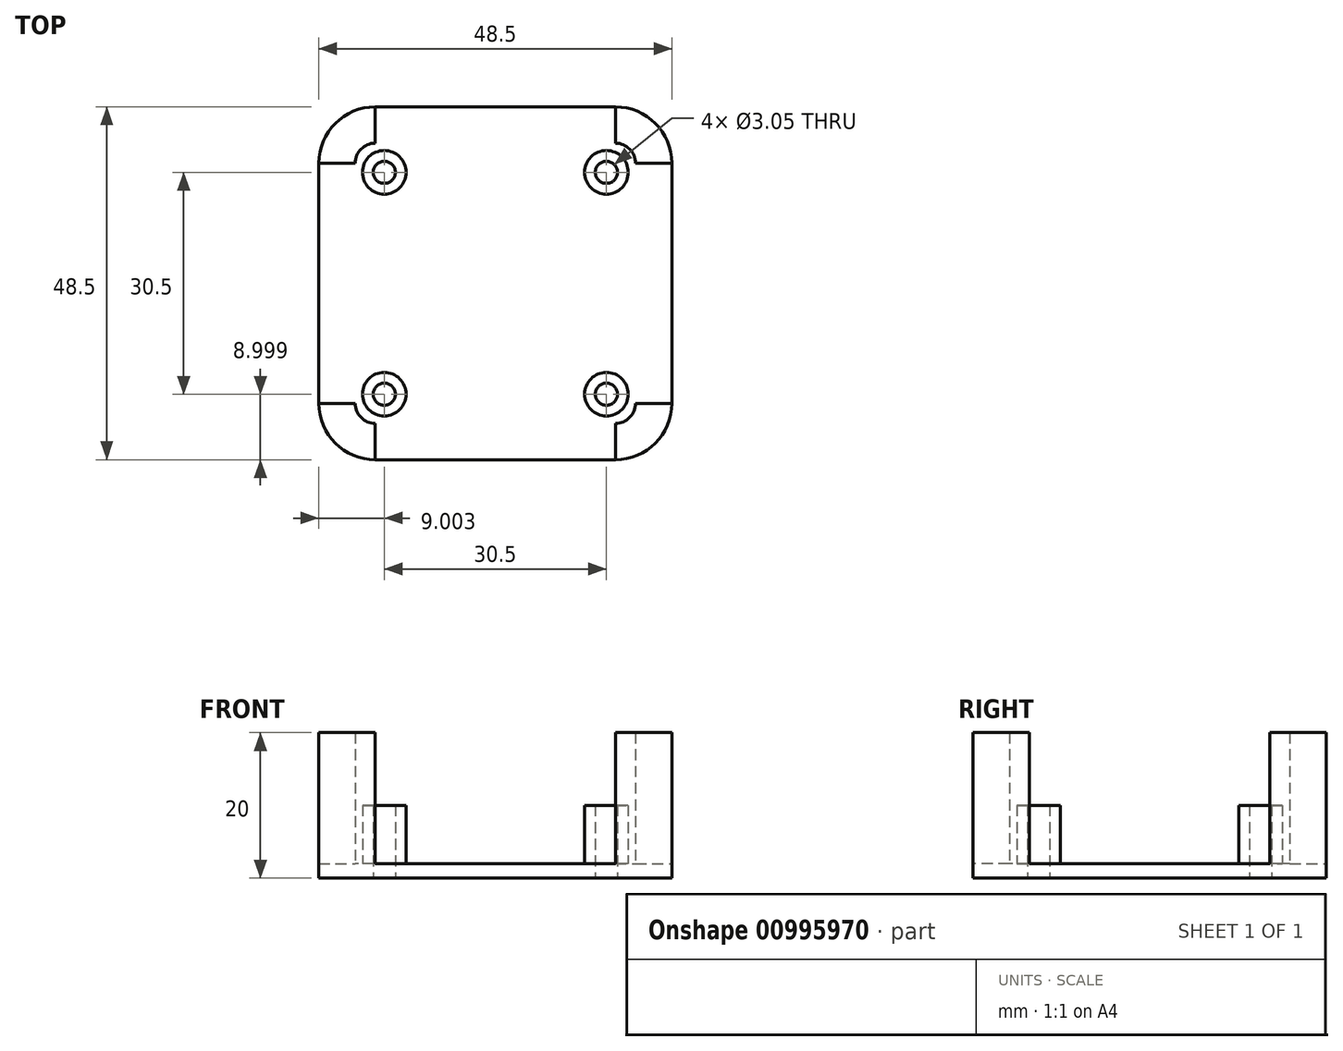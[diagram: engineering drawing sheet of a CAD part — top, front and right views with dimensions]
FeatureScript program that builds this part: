
annotation { "Feature Type Name" : "Feature", "Feature Type Description" : "" }
export const myFeature = defineFeature(function(context is Context, id is Id, definition is map)
    precondition{}
    {
        {
            var Q0;
            Q0=qCreatedBy(makeId("Top.planeOp"),FACE);
            var sketch = newSketch(context, id + "F0", { "sketchPlane" : qUnion([Q0])});
            skLineSegment(sketch, "E0.bottom", {"start": v(-15.03, 16.3) * mm, "end": v(17.97, 16.3) * mm});
            skLineSegment(sketch, "E0.top", {"start": v(-15.03, -22.2) * mm, "end": v(17.97, -22.2) * mm});
            skLineSegment(sketch, "E0.left", {"start": v(-17.78, 13.55) * mm, "end": v(-17.78, -19.45) * mm});
            skLineSegment(sketch, "E0.right", {"start": v(20.72, 13.55) * mm, "end": v(20.72, -19.45) * mm});
            skLineSegment(sketch, "E1.0", {"start": v(-13.78, 12.3) * mm, "end": v(-13.78, -18.2) * mm, "construction": true});
            skLineSegment(sketch, "E1.1", {"start": v(-13.78, 12.3) * mm, "end": v(16.72, 12.3) * mm, "construction": true});
            skLineSegment(sketch, "E1.2", {"start": v(16.72, 12.3) * mm, "end": v(16.72, -18.2) * mm, "construction": true});
            skLineSegment(sketch, "E1.3", {"start": v(-13.78, -18.2) * mm, "end": v(16.72, -18.2) * mm, "construction": true});
            skPoint(sketch, "E2.visualSharp", {"position": v(-17.78, 16.3) * mm});
            skArc(sketch, "E2.filletArc", {"start": v(-15.03, 16.3) * mm, "mid": v(-16.97, 15.5) * mm, "end": v(-17.78, 13.55) * mm});
            skPoint(sketch, "E3.visualSharp", {"position": v(20.72, 16.3) * mm});
            skArc(sketch, "E3.filletArc", {"start": v(20.72, 13.55) * mm, "mid": v(19.92, 15.5) * mm, "end": v(17.97, 16.3) * mm});
            skPoint(sketch, "E4.visualSharp", {"position": v(20.72, -22.2) * mm});
            skArc(sketch, "E4.filletArc", {"start": v(17.97, -22.2) * mm, "mid": v(19.92, -21.4) * mm, "end": v(20.72, -19.45) * mm});
            skPoint(sketch, "E5.visualSharp", {"position": v(-17.78, -22.2) * mm});
            skArc(sketch, "E5.filletArc", {"start": v(-17.78, -19.45) * mm, "mid": v(-16.97, -21.4) * mm, "end": v(-15.03, -22.2) * mm});
            skLineSegment(sketch, "E6.0", {"start": v(-22.78, 13.55) * mm, "end": v(-22.78, -19.45) * mm});
            skArc(sketch, "E6.1", {"start": v(-15.03, 21.3) * mm, "mid": v(-20.5, 19.03) * mm, "end": v(-22.78, 13.55) * mm});
            skArc(sketch, "E6.2", {"start": v(-22.78, -19.45) * mm, "mid": v(-20.5, -24.93) * mm, "end": v(-15.03, -27.2) * mm});
            skLineSegment(sketch, "E6.3", {"start": v(-15.03, 21.3) * mm, "end": v(17.97, 21.3) * mm});
            skLineSegment(sketch, "E6.4", {"start": v(-15.03, -27.2) * mm, "end": v(17.97, -27.2) * mm});
            skArc(sketch, "E6.5", {"start": v(17.97, -27.2) * mm, "mid": v(23.45, -24.93) * mm, "end": v(25.72, -19.45) * mm});
            skLineSegment(sketch, "E6.6", {"start": v(25.72, 13.55) * mm, "end": v(25.72, -19.45) * mm});
            skArc(sketch, "E6.7", {"start": v(25.72, 13.55) * mm, "mid": v(23.45, 19.03) * mm, "end": v(17.97, 21.3) * mm});
            skLineSegment(sketch, "E7", {"start": v(20.72, 13.55) * mm, "end": v(25.72, 13.55) * mm});
            skLineSegment(sketch, "E8", {"start": v(17.97, 16.3) * mm, "end": v(17.97, 21.3) * mm});
            skLineSegment(sketch, "E9", {"start": v(-15.03, 16.3) * mm, "end": v(-15.03, 21.3) * mm});
            skLineSegment(sketch, "E10", {"start": v(-22.78, 13.55) * mm, "end": v(-17.78, 13.55) * mm});
            skLineSegment(sketch, "E11", {"start": v(-15.03, -22.2) * mm, "end": v(-15.03, -27.2) * mm});
            skLineSegment(sketch, "E12", {"start": v(-17.78, -19.45) * mm, "end": v(-22.78, -19.45) * mm});
            skLineSegment(sketch, "E13", {"start": v(17.97, -22.2) * mm, "end": v(17.97, -27.2) * mm});
            skLineSegment(sketch, "E14", {"start": v(20.72, -19.45) * mm, "end": v(25.72, -19.45) * mm});
            skCircle(sketch, "E15", {"center": v(-13.78, -18.2) * mm, "radius": 3 * mm});
            skCircle(sketch, "E16", {"center": v(-13.78, -18.2) * mm, "radius": 1.52 * mm});
            skCircle(sketch, "E17.0.1.0", {"center": v(-13.78, 12.3) * mm, "radius": 3 * mm});
            skCircle(sketch, "E17.0.1.1", {"center": v(-13.78, 12.3) * mm, "radius": 1.52 * mm});
            skCircle(sketch, "E17.1.0.0", {"center": v(16.72, -18.2) * mm, "radius": 3 * mm});
            skCircle(sketch, "E17.1.0.1", {"center": v(16.72, -18.2) * mm, "radius": 1.52 * mm});
            skCircle(sketch, "E17.1.1.0", {"center": v(16.72, 12.3) * mm, "radius": 3 * mm});
            skCircle(sketch, "E17.1.1.1", {"center": v(16.72, 12.3) * mm, "radius": 1.52 * mm});
            skLineSegment(sketch, "E17.direction2", {"start": v(-13.78, -18.2) * mm, "end": v(-13.78, 12.3) * mm, "construction": true});
            skSolve(sketch);
        }
        {
            var Q0;
            Q0=makeQuery(id+"F0.imprint","IMPRINT",FACE,{"disambiguationData":[TD([[makeQuery(id+"F0.imprint","IMPRINT",EDGE,{"derivedFrom":sQuery(id+"F0.wireOp",EDGE,"E0.bottom")}),1.0]])]});
            var Q1;
            Q1=makeQuery(id+"F0.imprint","IMPRINT",FACE,{"disambiguationData":[TD([[makeQuery(id+"F0.imprint","IMPRINT",EDGE,{"derivedFrom":sQuery(id+"F0.wireOp",EDGE,"E6.0")}),1.0]])]});
            var Q2;
            Q2=makeQuery(id+"F0.imprint","IMPRINT",FACE,{"disambiguationData":[TD([[makeQuery(id+"F0.imprint","IMPRINT",EDGE,{"derivedFrom":sQuery(id+"F0.wireOp",EDGE,"E0.bottom")}),-1.0]])]});
            var Q3;
            Q3=makeQuery(id+"F0.imprint","IMPRINT",FACE,{"disambiguationData":[TD([[makeQuery(id+"F0.imprint","IMPRINT",EDGE,{"derivedFrom":sQuery(id+"F0.wireOp",EDGE,"E0.right")}),1.0]])]});
            var Q4;
            Q4=makeQuery(id+"F0.imprint","IMPRINT",FACE,{"disambiguationData":[TD([[makeQuery(id+"F0.imprint","IMPRINT",EDGE,{"derivedFrom":sQuery(id+"F0.wireOp",EDGE,"E0.top")}),-1.0]])]});
            extrude(context, id + "F1", {"entities" : qUnion([Q0, Q1, Q2, Q3, Q4]), "depth" : 2 * mm, "offsetDistance" : 25 * mm});
        }
        {
            var Q0;
            Q0=makeQuery(id+"F0.imprint","IMPRINT",FACE,{"disambiguationData":[TD([[makeQuery(id+"F0.imprint","IMPRINT",EDGE,{"derivedFrom":sQuery(id+"F0.wireOp",EDGE,"E2.filletArc")}),-1.0]])]});
            var Q1;
            Q1=makeQuery(id+"F0.imprint","IMPRINT",FACE,{"disambiguationData":[TD([[makeQuery(id+"F0.imprint","IMPRINT",EDGE,{"derivedFrom":sQuery(id+"F0.wireOp",EDGE,"E3.filletArc")}),-1.0]])]});
            var Q2;
            Q2=makeQuery(id+"F0.imprint","IMPRINT",FACE,{"disambiguationData":[TD([[makeQuery(id+"F0.imprint","IMPRINT",EDGE,{"derivedFrom":sQuery(id+"F0.wireOp",EDGE,"E4.filletArc")}),-1.0]])]});
            var Q3;
            Q3=makeQuery(id+"F0.imprint","IMPRINT",FACE,{"disambiguationData":[TD([[makeQuery(id+"F0.imprint","IMPRINT",EDGE,{"derivedFrom":sQuery(id+"F0.wireOp",EDGE,"E5.filletArc")}),-1.0]])]});
            extrude(context, id + "F2", {"entities" : qUnion([Q0, Q1, Q2, Q3]), "operationType" : NewBodyOperationType.ADD, "depth" : 20 * mm, "offsetDistance" : 25 * mm});
        }
        {
            var Q0;
            Q0=makeQuery(id+"F0.imprint","IMPRINT",FACE,{"disambiguationData":[TD([[makeQuery(id+"F0.imprint","IMPRINT",EDGE,{"derivedFrom":sQuery(id+"F0.wireOp",EDGE,"E17.0.1.0")}),1.0]])]});
            var Q1;
            Q1=makeQuery(id+"F0.imprint","IMPRINT",FACE,{"disambiguationData":[TD([[makeQuery(id+"F0.imprint","IMPRINT",EDGE,{"derivedFrom":sQuery(id+"F0.wireOp",EDGE,"E17.1.1.0")}),1.0]])]});
            var Q2;
            Q2=makeQuery(id+"F0.imprint","IMPRINT",FACE,{"disambiguationData":[TD([[makeQuery(id+"F0.imprint","IMPRINT",EDGE,{"derivedFrom":sQuery(id+"F0.wireOp",EDGE,"E17.1.0.0")}),1.0]])]});
            var Q3;
            Q3=makeQuery(id+"F0.imprint","IMPRINT",FACE,{"disambiguationData":[TD([[makeQuery(id+"F0.imprint","IMPRINT",EDGE,{"derivedFrom":sQuery(id+"F0.wireOp",EDGE,"E15")}),1.0]])]});
            extrude(context, id + "F3", {"entities" : qUnion([Q0, Q1, Q2, Q3]), "operationType" : NewBodyOperationType.ADD, "depth" : 10 * mm, "offsetDistance" : 25 * mm});
        }
    });
